# Revit family: Faucet-Wall_Mount-Lavatory-KOHLER-PARALLEL-K-23485T_1
name_source: partatom
category: Plumbing Fixtures
revit_build: Autodesk Revit 2017 (Build: 20160225_1515(x64)
units: mm (PartAtom-declared; Revit-internal decimal feet)

## family parameters
Cut with Voids When Loaded = No
Host = Face
OmniClass Number = 23.31.11.00
OmniClass Title = Faucets
Part Type = Normal
Room Calculation Point = No
Round Connector Dimension = Use Diameter
Shared = No

## types (6) — shared parameters
ADA Compliant = No
Assembly Code = D2010
CW Connection = Yes
Cold Water Inlet = Cold Water Inlet
Date Modified = 06/18/2020
Default Elevation = 36"
Flow Rate = 2 GPM
HW Connection = Yes
Handle Clearance = 3 13/16"
Height = 3 1/8"
Hot Water Inlet = Hot Water Inlet
Length = 6 1/2"
Manufacturer = KOHLER Co.
Master Format 2014 = 22 41 39
Master Format 2014 Name = Residential Faucets, Supplies, and Trim
Material = Premium Metal Construction
Pressure = 60.00 psi
Product Name = PARALLEL
Spout Reach = 6 1/2"
URL = http://www.kohler.com.cn
Vent Connection = No
Waste Connection = No
Waste Water Outlet = Waste Water Outlet
WaterSense Certified = No
Width = 7 5/8"

## per-type parameters (varying)
| type | Description | Drain Included | Finish | Model | Product Documentation Link | Product Page URL | Type |
| CP-Polished Chrome | Ruofang single-handle faucet for wall outlet (outlet nozzle length 165mm) | Yes | Kohler-Metal-CP-Polished_Chrome | K-23485T-4-CP | https://files.kohler.com.cn | https://www.kohler.com.cn | 1 |
| AF-Flange Gold | Ruofang single-handle faucet for wall outlet (outlet nozzle length 165mm) | Yes | Kohler-Metal-AF-Flange_Gold | K-23485T-4-AF | https://files.kohler.com.cn | https://www.kohler.com.cn | 2 |
| BN-Roman Silver | Ruofang single-handle faucet for wall outlet (outlet nozzle length 165mm) | Yes | Kohler-Metal-BN-Roman_Silver | K-23485T-4-BN | https://files.kohler.com.cn | https://www.kohler.com.cn | 3 |
| RGD-Rose Gold | Ruofang single-handle faucet for wall outlet (outlet nozzle length 165mm) | Yes | Kohler-Metal-RGD-Rose_Gold | K-23485T-4-RGD | https://files.kohler.com.cn | https://www.kohler.com.cn | 4 |
| BL-Matte Black | Ruofang single-handle faucet for wall outlet (outlet nozzle length 165mm) | Yes | Kohler-Metal-BL-Matte_Black | K-23485T-4-BL | https://files.kohler.com.cn | https://www.kohler.com.cn | 5 |
| No Drain, CP-Polished Chrome | Ruofang single-handle faucet for wall outlet-No Drain | No | Kohler-Metal-CP-Polished_Chrome | K-23485T-4ND-CP |  |  | 6 |

## geometry (parser evidence)
native form markers: Sweep x4
no freeform markers — native parametric forms only
